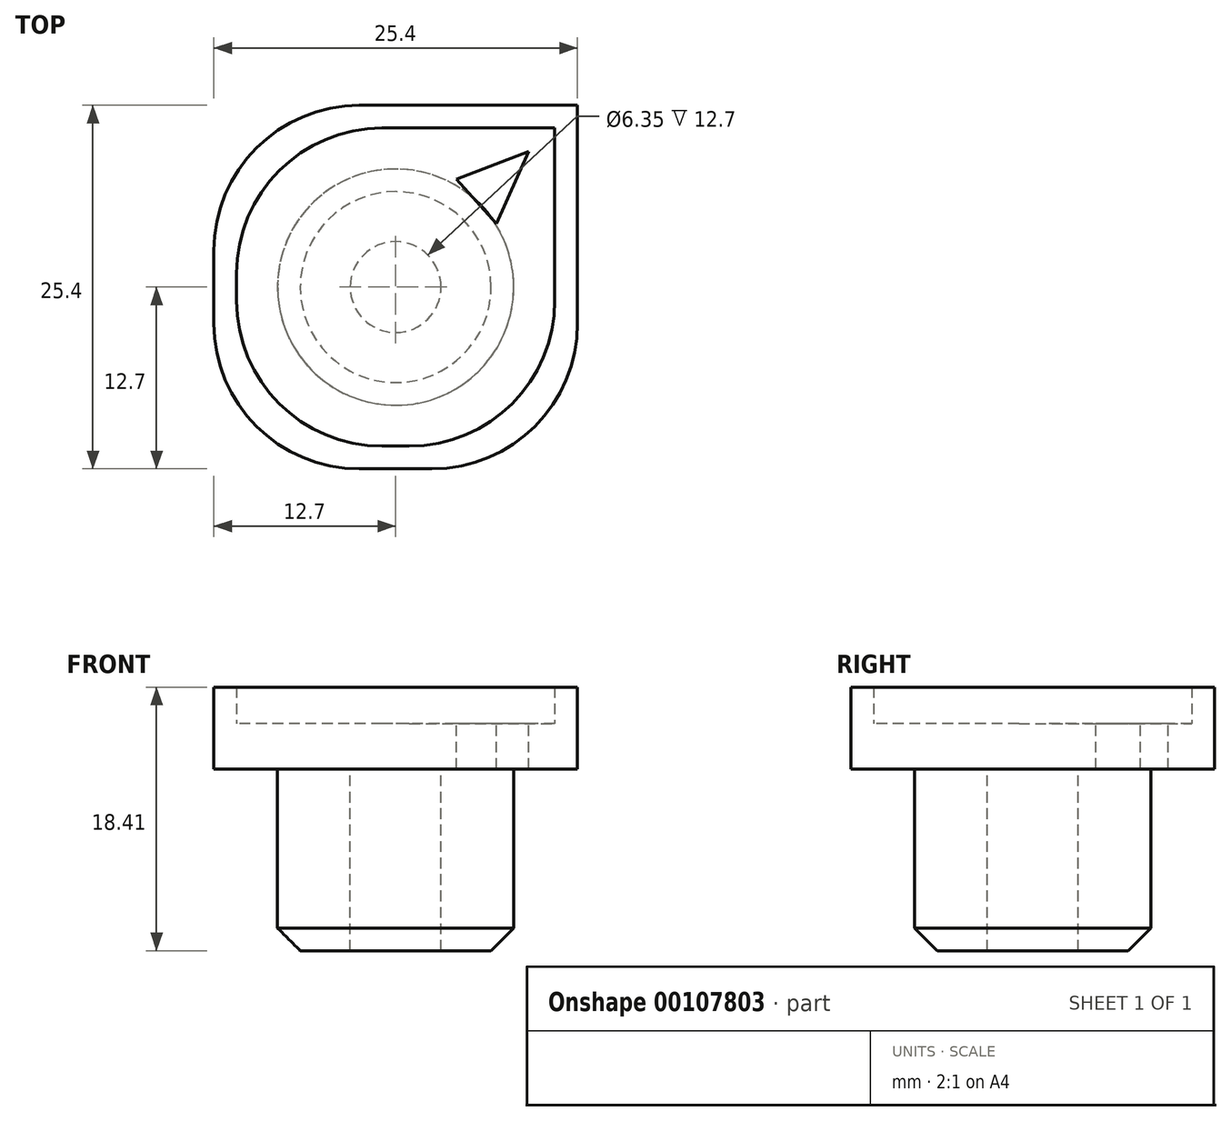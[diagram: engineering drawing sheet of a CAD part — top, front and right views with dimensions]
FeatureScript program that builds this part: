
annotation { "Feature Type Name" : "Feature", "Feature Type Description" : "" }
export const myFeature = defineFeature(function(context is Context, id is Id, definition is map)
    precondition{}
    {
        {
            var Q0;
            Q0=qCreatedBy(makeId("Top.planeOp"),FACE);
            var sketch = newSketch(context, id + "F0", { "sketchPlane" : qUnion([Q0])});
            skLineSegment(sketch, "E0.bottom", {"start": v(12.7, -12.7) * mm, "end": v(-12.7, -12.7) * mm});
            skLineSegment(sketch, "E0.top", {"start": v(12.7, 12.7) * mm, "end": v(-12.7, 12.7) * mm});
            skLineSegment(sketch, "E0.left", {"start": v(12.7, -12.7) * mm, "end": v(12.7, 12.7) * mm});
            skLineSegment(sketch, "E0.right", {"start": v(-12.7, -12.7) * mm, "end": v(-12.7, 12.7) * mm});
            skPoint(sketch, "E0.middle", {"position": v(0, 0) * mm});
            skSolve(sketch);
        }
        {
            var Q0;
            Q0 = qSketchRegion(id + "F0", true);
            extrude(context, id + "F1", {"entities" : qUnion([Q0]), "depth" : 3.17 * mm});
        }
        {
            var Q0;
            Q0=makeQuery(id+"F1.opExtrude","CAP_FACE",FACE,{"disambiguationData":[OSD([sQuery(id+"F0.wireOp",EDGE,"E0.bottom"),sQuery(id+"F0.wireOp",EDGE,"E0.top"),sQuery(id+"F0.wireOp",EDGE,"E0.left"),sQuery(id+"F0.wireOp",EDGE,"E0.right")])],"isStart":false});
            var sketch = newSketch(context, id + "F2", { "sketchPlane" : qUnion([Q0])});
            skLineSegment(sketch, "E1.0.0", {"start": v(-12.7, -12.7) * mm, "end": v(12.7, -12.7) * mm});
            skLineSegment(sketch, "E1.0.1", {"start": v(12.7, -12.7) * mm, "end": v(12.7, 12.7) * mm});
            skLineSegment(sketch, "E1.0.2", {"start": v(12.7, 12.7) * mm, "end": v(-12.7, 12.7) * mm});
            skLineSegment(sketch, "E1.0.3", {"start": v(-12.7, 12.7) * mm, "end": v(-12.7, -12.7) * mm});
            skLineSegment(sketch, "E2.bottom", {"start": v(11.11, -11.11) * mm, "end": v(-11.11, -11.11) * mm});
            skLineSegment(sketch, "E2.top", {"start": v(11.11, 11.11) * mm, "end": v(-11.11, 11.11) * mm});
            skLineSegment(sketch, "E2.left", {"start": v(11.11, -11.11) * mm, "end": v(11.11, 11.11) * mm});
            skLineSegment(sketch, "E2.right", {"start": v(-11.11, -11.11) * mm, "end": v(-11.11, 11.11) * mm});
            skPoint(sketch, "E2.middle", {"position": v(0, 0) * mm});
            skSolve(sketch);
        }
        {
            var Q0;
            Q0 = qSketchRegion(id + "F2", true);
            extrude(context, id + "F3", {"entities" : qUnion([Q0]), "operationType" : NewBodyOperationType.ADD, "depth" : 2.54 * mm});
        }
        {
            var Q0;
            Q0=makeQuery(id+"F1.opExtrude","CAP_FACE",FACE,{"disambiguationData":[OSD([sQuery(id+"F0.wireOp",EDGE,"E0.bottom"),sQuery(id+"F0.wireOp",EDGE,"E0.top"),sQuery(id+"F0.wireOp",EDGE,"E0.left"),sQuery(id+"F0.wireOp",EDGE,"E0.right")])],"isStart":false});
            var sketch = newSketch(context, id + "F4", { "sketchPlane" : qUnion([Q0])});
            skLineSegment(sketch, "E3", {"start": v(9.3, 9.49) * mm, "end": v(4.24, 7.55) * mm});
            skLineSegment(sketch, "E4", {"start": v(4.24, 7.55) * mm, "end": v(9.3, 9.49) * mm});
            skLineSegment(sketch, "E5", {"start": v(9.3, 9.49) * mm, "end": v(7.03, 4.43) * mm});
            skLineSegment(sketch, "E6", {"start": v(7.03, 4.43) * mm, "end": v(4.24, 7.55) * mm});
            skLineSegment(sketch, "E7", {"start": v(-1.3, 0) * mm, "end": v(11.11, 11.11) * mm, "construction": true});
            skSolve(sketch);
        }
        {
            var Q0;
            Q0 = qSketchRegion(id + "F4", true);
            extrude(context, id + "F5", {"entities" : qUnion([Q0]), "operationType" : NewBodyOperationType.REMOVE, "oppositeDirection" : true, "depth" : 25.4 * mm});
        }
        {
            var Q0;
            Q0=makeQuery(id+"F1.opExtrude","CAP_FACE",FACE,{"disambiguationData":[OSD([sQuery(id+"F0.wireOp",EDGE,"E0.bottom"),sQuery(id+"F0.wireOp",EDGE,"E0.top"),sQuery(id+"F0.wireOp",EDGE,"E0.left"),sQuery(id+"F0.wireOp",EDGE,"E0.right")])],"isStart":true});
            var sketch = newSketch(context, id + "F6", { "sketchPlane" : qUnion([Q0])});
            skCircle(sketch, "E8", {"center": v(0, 0) * mm, "radius": 8.26 * mm});
            skCircle(sketch, "E9", {"center": v(0, 0) * mm, "radius": 3.18 * mm});
            skSolve(sketch);
        }
        {
            var Q0;
            Q0 = qSketchRegion(id + "F6", true);
            extrude(context, id + "F7", {"entities" : qUnion([Q0]), "operationType" : NewBodyOperationType.ADD, "depth" : 12.7 * mm});
        }
        {
            var Q0;
            Q0=makeQuery(id+"F3.boolean.opBoolean","MERGE",EDGE,{"derivedFrom":[makeQuery(id+"F1.opExtrude","SWEPT_EDGE",EDGE,{"disambiguationData":[OSD([sQuery(id+"F0.wireOp",EDGE,"E0.bottom"),sQuery(id+"F0.wireOp",EDGE,"E0.left")])]}),makeQuery(id+"F3.opExtrude","SWEPT_EDGE",EDGE,{"disambiguationData":[OSD([sQuery(id+"F2.wireOp",EDGE,"E1.0.0"),sQuery(id+"F2.wireOp",EDGE,"E1.0.1")])]})]});
            var Q1;
            Q1=makeQuery(id+"F3.boolean.opBoolean","MERGE",EDGE,{"derivedFrom":[makeQuery(id+"F1.opExtrude","SWEPT_EDGE",EDGE,{"disambiguationData":[OSD([sQuery(id+"F0.wireOp",EDGE,"E0.bottom"),sQuery(id+"F0.wireOp",EDGE,"E0.right")])]}),makeQuery(id+"F3.opExtrude","SWEPT_EDGE",EDGE,{"disambiguationData":[OSD([sQuery(id+"F2.wireOp",EDGE,"E1.0.0"),sQuery(id+"F2.wireOp",EDGE,"E1.0.3")])]})]});
            var Q2;
            Q2=makeQuery(id+"F3.opExtrude","SWEPT_EDGE",EDGE,{"disambiguationData":[OSD([sQuery(id+"F2.wireOp",EDGE,"E2.bottom"),sQuery(id+"F2.wireOp",EDGE,"E2.right")])]});
            var Q3;
            Q3=makeQuery(id+"F3.opExtrude","SWEPT_EDGE",EDGE,{"disambiguationData":[OSD([sQuery(id+"F2.wireOp",EDGE,"E2.bottom"),sQuery(id+"F2.wireOp",EDGE,"E2.left")])]});
            var Q4;
            Q4=makeQuery(id+"F3.opExtrude","SWEPT_EDGE",EDGE,{"disambiguationData":[OSD([sQuery(id+"F2.wireOp",EDGE,"E2.top"),sQuery(id+"F2.wireOp",EDGE,"E2.right")])]});
            var Q5;
            Q5=makeQuery(id+"F3.boolean.opBoolean","MERGE",EDGE,{"derivedFrom":[makeQuery(id+"F1.opExtrude","SWEPT_EDGE",EDGE,{"disambiguationData":[OSD([sQuery(id+"F0.wireOp",EDGE,"E0.top"),sQuery(id+"F0.wireOp",EDGE,"E0.right")])]}),makeQuery(id+"F3.opExtrude","SWEPT_EDGE",EDGE,{"disambiguationData":[OSD([sQuery(id+"F2.wireOp",EDGE,"E1.0.2"),sQuery(id+"F2.wireOp",EDGE,"E1.0.3")])]})]});
            fillet(context, id + "F8", {"entities" : qUnion([Q0, Q1, Q2, Q3, Q4, Q5]), "radius" : 10.16 * mm, "tangentPropagation" : true, "allowEdgeOverflow" : false});
        }
        {
            var Q0;
            Q0=makeQuery(id+"F7.opExtrude","CAP_EDGE",EDGE,{"disambiguationData":[OSD([sQuery(id+"F6.wireOp",EDGE,"E8")])],"isStart":false});
            chamfer(context, id + "F9", {"entities" : qUnion([Q0]), "width" : 1.59 * mm, "tangentPropagation" : true});
        }
    });
